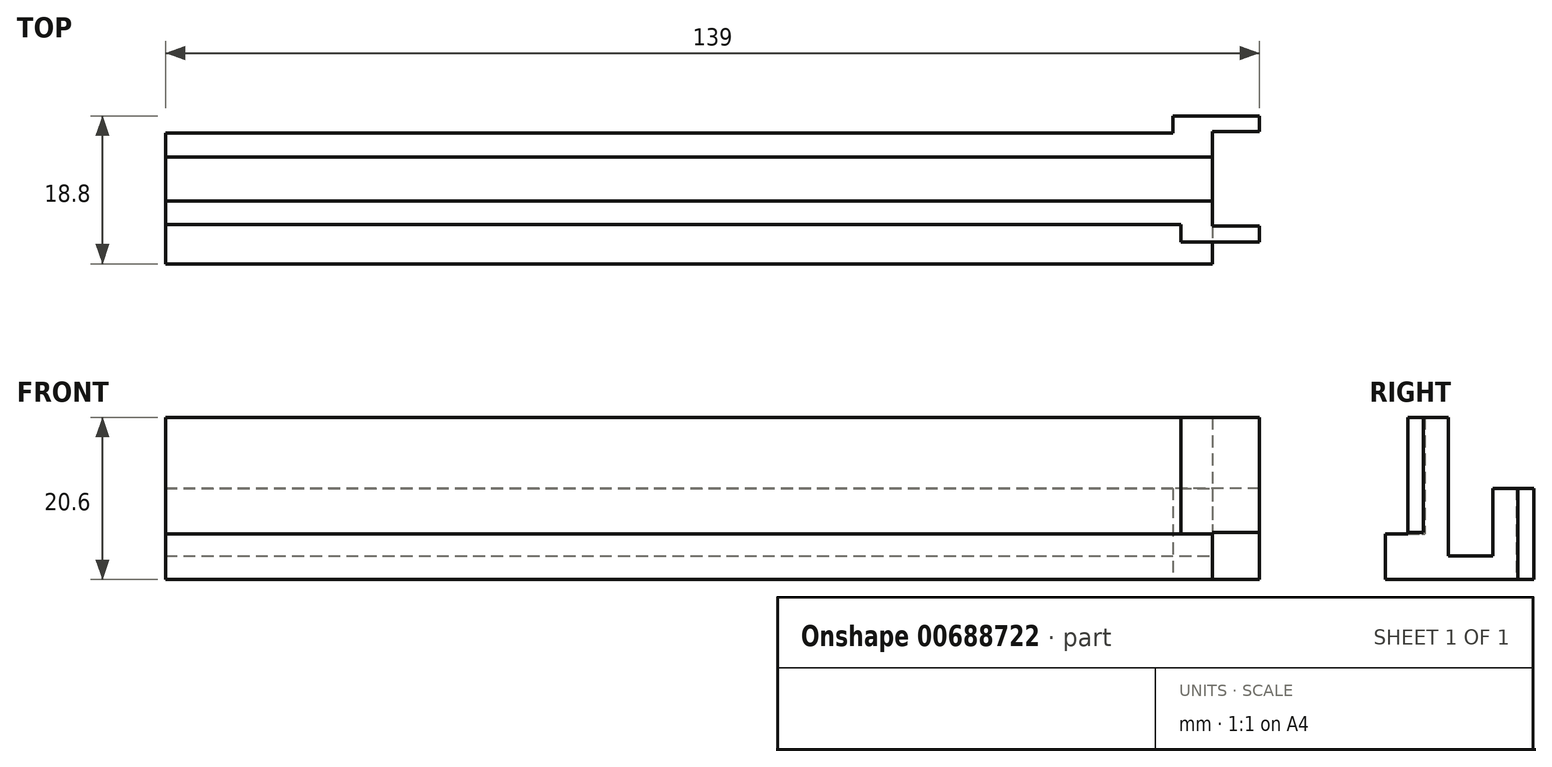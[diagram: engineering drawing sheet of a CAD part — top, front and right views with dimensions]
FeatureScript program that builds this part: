
annotation { "Feature Type Name" : "Feature", "Feature Type Description" : "" }
export const myFeature = defineFeature(function(context is Context, id is Id, definition is map)
    precondition{}
    {
        {
            var Q0;
            Q0=qCreatedBy(makeId("Front.planeOp"),FACE);
            var sketch = newSketch(context, id + "F0", { "sketchPlane" : qUnion([Q0])});
            skLineSegment(sketch, "E0.bottom", {"start": v(66.5, 5.8) * mm, "end": v(-66.5, 5.8) * mm});
            skLineSegment(sketch, "E0.top", {"start": v(66.5, -5.8) * mm, "end": v(-66.5, -5.8) * mm});
            skLineSegment(sketch, "E0.left", {"start": v(66.5, 5.8) * mm, "end": v(66.5, -5.8) * mm});
            skLineSegment(sketch, "E0.right", {"start": v(-66.5, 5.8) * mm, "end": v(-66.5, -5.8) * mm});
            skPoint(sketch, "E0.middle", {"position": v(0, 0) * mm});
            skSolve(sketch);
        }
        {
            var Q0;
            Q0 = qSketchRegion(id + "F0", true);
            extrude(context, id + "F1", {"entities" : qUnion([Q0]), "depth" : 11.6 * mm, "offsetDistance" : 25 * mm});
        }
        {
            var Q0;
            Q0=makeQuery(id+"F1.opExtrude","SWEPT_FACE",FACE,{"disambiguationData":[OSD([sQuery(id+"F0.wireOp",EDGE,"E0.left")])]});
            var sketch = newSketch(context, id + "F2", { "sketchPlane" : qUnion([Q0])});
            skLineSegment(sketch, "E1", {"start": v(-8.6, 5.8) * mm, "end": v(-8.6, -5.8) * mm});
            skLineSegment(sketch, "E2", {"start": v(-3, 5.8) * mm, "end": v(-3, -5.8) * mm});
            skLineSegment(sketch, "E3", {"start": v(-11.6, -2.8) * mm, "end": v(0, -2.8) * mm, "construction": true});
            skLineSegment(sketch, "E4", {"start": v(-8.6, -2.8) * mm, "end": v(-3, -2.8) * mm});
            skSolve(sketch);
        }
        {
            var Q0;
            {var subQ3=sQuery(id+"F2.wireOp",EDGE,"E4");Q0=makeQuery(id+"F2.imprint","IMPRINT",FACE,{"disambiguationData":[TD([[makeQuery(id+"F2.imprint","IMPRINT",EDGE,{"derivedFrom":subQ3}),1.0]])]});}
            extrude(context, id + "F3", {"entities" : qUnion([Q0]), "operationType" : NewBodyOperationType.REMOVE, "oppositeDirection" : true, "depth" : 133 * mm, "offsetDistance" : 25 * mm});
        }
        {
            var Q0;
            {var subQ2=sQuery(id+"F0.wireOp",EDGE,"E0.bottom");Q0=makeQuery(id+"F3.boolean.opBoolean","SPLIT",FACE,{"disambiguationData":[TD([makeQuery(id+"F3.opExtrude","SWEPT_FACE",FACE,{"disambiguationData":[OSD([sQuery(id+"F2.wireOp",EDGE,"E1")])]})])],"derivedFrom":makeQuery(id+"F1.opExtrude","SWEPT_FACE",FACE,{"disambiguationData":[OSD([subQ2])]})});}
            extrude(context, id + "F4", {"entities" : qUnion([Q0]), "operationType" : NewBodyOperationType.ADD, "depth" : 9 * mm, "offsetDistance" : 25 * mm});
        }
        {
            var Q0;
            {var subQ0=sQuery(id+"F0.wireOp",EDGE,"E0.bottom");Q0=makeQuery(id+"F4.boolean.opBoolean","MERGE",FACE,{"derivedFrom":[makeQuery(id+"F1.opExtrude","CAP_FACE",FACE,{"disambiguationData":[OSD([subQ0,sQuery(id+"F0.wireOp",EDGE,"E0.top"),sQuery(id+"F0.wireOp",EDGE,"E0.left"),sQuery(id+"F0.wireOp",EDGE,"E0.right")])],"isStart":false}),makeQuery(id+"F4.opExtrude","SWEPT_FACE",FACE,{"disambiguationData":[OSD([subQ0])]})]});}
            var sketch = newSketch(context, id + "F5", { "sketchPlane" : qUnion([Q0])});
            skLineSegment(sketch, "E5", {"start": v(-66.5, 0) * mm, "end": v(66.5, 0) * mm});
            skSolve(sketch);
        }
        {
            var Q0;
            {var subQ0=sQuery(id+"F5.wireOp",EDGE,"E5");Q0=makeQuery(id+"F5.imprint","IMPRINT",FACE,{"disambiguationData":[TD([[makeQuery(id+"F5.imprint","IMPRINT",EDGE,{"derivedFrom":subQ0}),-1.0]])]});}
            extrude(context, id + "F6", {"entities" : qUnion([Q0]), "operationType" : NewBodyOperationType.ADD, "depth" : 5 * mm, "offsetDistance" : 25 * mm});
        }
        {
            var Q0;
            {var subQ0=sQuery(id+"F0.wireOp",EDGE,"E0.bottom");Q0=makeQuery(id+"F4.boolean.opBoolean","MERGE",FACE,{"derivedFrom":[makeQuery(id+"F1.opExtrude","CAP_FACE",FACE,{"disambiguationData":[OSD([subQ0,sQuery(id+"F0.wireOp",EDGE,"E0.top"),sQuery(id+"F0.wireOp",EDGE,"E0.left"),sQuery(id+"F0.wireOp",EDGE,"E0.right")])],"isStart":false}),makeQuery(id+"F4.opExtrude","SWEPT_FACE",FACE,{"disambiguationData":[OSD([subQ0])]})]});}
            var sketch = newSketch(context, id + "F7", { "sketchPlane" : qUnion([Q0])});
            skLineSegment(sketch, "E6", {"start": v(0, 0) * mm, "end": v(0, 14.8) * mm});
            skSolve(sketch);
        }
        {
            var Q0;
            {var subQ0=sQuery(id+"F7.wireOp",EDGE,"E6");Q0=makeQuery(id+"F7.imprint","IMPRINT",FACE,{"disambiguationData":[TD([[makeQuery(id+"F7.imprint","IMPRINT",EDGE,{"derivedFrom":subQ0}),-1.0]])]});}
            var sketch = newSketch(context, id + "F8", { "sketchPlane" : qUnion([Q0])});
            skLineSegment(sketch, "E7", {"start": v(62.5, 14.8) * mm, "end": v(62.5, 0) * mm});
            skSolve(sketch);
        }
        {
            var Q0;
            {var subQ0=sQuery(id+"F8.wireOp",EDGE,"E7");Q0=makeQuery(id+"F8.imprint","IMPRINT",FACE,{"disambiguationData":[TD([[makeQuery(id+"F8.imprint","IMPRINT",EDGE,{"derivedFrom":subQ0}),1.0]])]});}
            extrude(context, id + "F9", {"entities" : qUnion([Q0]), "operationType" : NewBodyOperationType.ADD, "depth" : 2.2 * mm, "offsetDistance" : 25 * mm});
        }
        {
            var Q0;
            {var subQ0=sQuery(id+"F0.wireOp",EDGE,"E0.left");var subQ1=sQuery(id+"F0.wireOp",EDGE,"E0.bottom");Q0=makeQuery(id+"F9.boolean.opBoolean","MERGE",FACE,{"derivedFrom":[makeQuery(id+"F6.boolean.opBoolean","MERGE",FACE,{"derivedFrom":[makeQuery(id+"F4.boolean.opBoolean","MERGE",FACE,{"derivedFrom":[makeQuery(id+"F1.opExtrude","SWEPT_FACE",FACE,{"disambiguationData":[OSD([subQ0])]}),makeQuery(id+"F4.opExtrude","SWEPT_FACE",FACE,{"disambiguationData":[OSD([subQ1,subQ0])]})]}),makeQuery(id+"F6.opExtrude","SWEPT_FACE",FACE,{"disambiguationData":[OSD([subQ1,subQ0])]})]}),makeQuery(id+"F9.opExtrude","SWEPT_FACE",FACE,{"disambiguationData":[OSD([subQ1,subQ0])]})]});}
            var sketch = newSketch(context, id + "F10", { "sketchPlane" : qUnion([Q0])});
            skLineSegment(sketch, "E8", {"start": v(-11.8, 14.8) * mm, "end": v(-11.8, 0.2) * mm});
            skLineSegment(sketch, "E9", {"start": v(-11.8, 0.2) * mm, "end": v(-13.8, 0.2) * mm});
            skPoint(sketch, "E10.end.orphan", {"position": v(-13.8, 0) * mm});
            skPoint(sketch, "E11.orphan", {"position": v(-11.8, 0) * mm});
            skSolve(sketch);
        }
        {
            var Q0;
            {var subQ0=sQuery(id+"F10.wireOp",EDGE,"E8");Q0=makeQuery(id+"F10.imprint","IMPRINT",FACE,{"disambiguationData":[TD([[makeQuery(id+"F10.imprint","IMPRINT",EDGE,{"derivedFrom":subQ0}),-1.0]])]});}
            extrude(context, id + "F11", {"entities" : qUnion([Q0]), "operationType" : NewBodyOperationType.ADD, "depth" : 6 * mm, "offsetDistance" : 25 * mm});
        }
        {
            var Q0;
            Q0=makeQuery(id+"F1.opExtrude","CAP_FACE",FACE,{"disambiguationData":[OSD([sQuery(id+"F0.wireOp",EDGE,"E0.bottom"),sQuery(id+"F0.wireOp",EDGE,"E0.top"),sQuery(id+"F0.wireOp",EDGE,"E0.left"),sQuery(id+"F0.wireOp",EDGE,"E0.right")])],"isStart":true});
            var sketch = newSketch(context, id + "F12", { "sketchPlane" : qUnion([Q0])});
            skLineSegment(sketch, "E12", {"start": v(-61.5, 5.8) * mm, "end": v(-61.5, -5.8) * mm});
            skSolve(sketch);
        }
        {
            var Q0;
            {var subQ0=sQuery(id+"F12.wireOp",EDGE,"E12");Q0=makeQuery(id+"F12.imprint","IMPRINT",FACE,{"disambiguationData":[TD([[makeQuery(id+"F12.imprint","IMPRINT",EDGE,{"derivedFrom":subQ0}),-1.0]])]});}
            extrude(context, id + "F13", {"entities" : qUnion([Q0]), "operationType" : NewBodyOperationType.ADD, "depth" : 2.2 * mm, "offsetDistance" : 25 * mm});
        }
        {
            var Q0;
            {var subQ0=sQuery(id+"F0.wireOp",EDGE,"E0.left");var subQ1=sQuery(id+"F0.wireOp",EDGE,"E0.bottom");Q0=makeQuery(id+"F13.boolean.opBoolean","MERGE",FACE,{"derivedFrom":[makeQuery(id+"F9.boolean.opBoolean","MERGE",FACE,{"derivedFrom":[makeQuery(id+"F6.boolean.opBoolean","MERGE",FACE,{"derivedFrom":[makeQuery(id+"F4.boolean.opBoolean","MERGE",FACE,{"derivedFrom":[makeQuery(id+"F1.opExtrude","SWEPT_FACE",FACE,{"disambiguationData":[OSD([subQ0])]}),makeQuery(id+"F4.opExtrude","SWEPT_FACE",FACE,{"disambiguationData":[OSD([subQ1,subQ0])]})]}),makeQuery(id+"F6.opExtrude","SWEPT_FACE",FACE,{"disambiguationData":[OSD([subQ1,subQ0])]})]}),makeQuery(id+"F9.opExtrude","SWEPT_FACE",FACE,{"disambiguationData":[OSD([subQ1,subQ0])]})]}),makeQuery(id+"F13.opExtrude","SWEPT_FACE",FACE,{"disambiguationData":[OSD([subQ0])]})]});}
            var sketch = newSketch(context, id + "F14", { "sketchPlane" : qUnion([Q0])});
            skLineSegment(sketch, "E13", {"start": v(0.2, 5.8) * mm, "end": v(0.2, -5.8) * mm});
            skSolve(sketch);
        }
        {
            var Q0;
            {var subQ0=sQuery(id+"F14.wireOp",EDGE,"E13");Q0=makeQuery(id+"F14.imprint","IMPRINT",FACE,{"disambiguationData":[TD([[makeQuery(id+"F14.imprint","IMPRINT",EDGE,{"derivedFrom":subQ0}),1.0]])]});}
            extrude(context, id + "F15", {"entities" : qUnion([Q0]), "operationType" : NewBodyOperationType.ADD, "depth" : 6 * mm, "offsetDistance" : 25 * mm});
        }
    });
